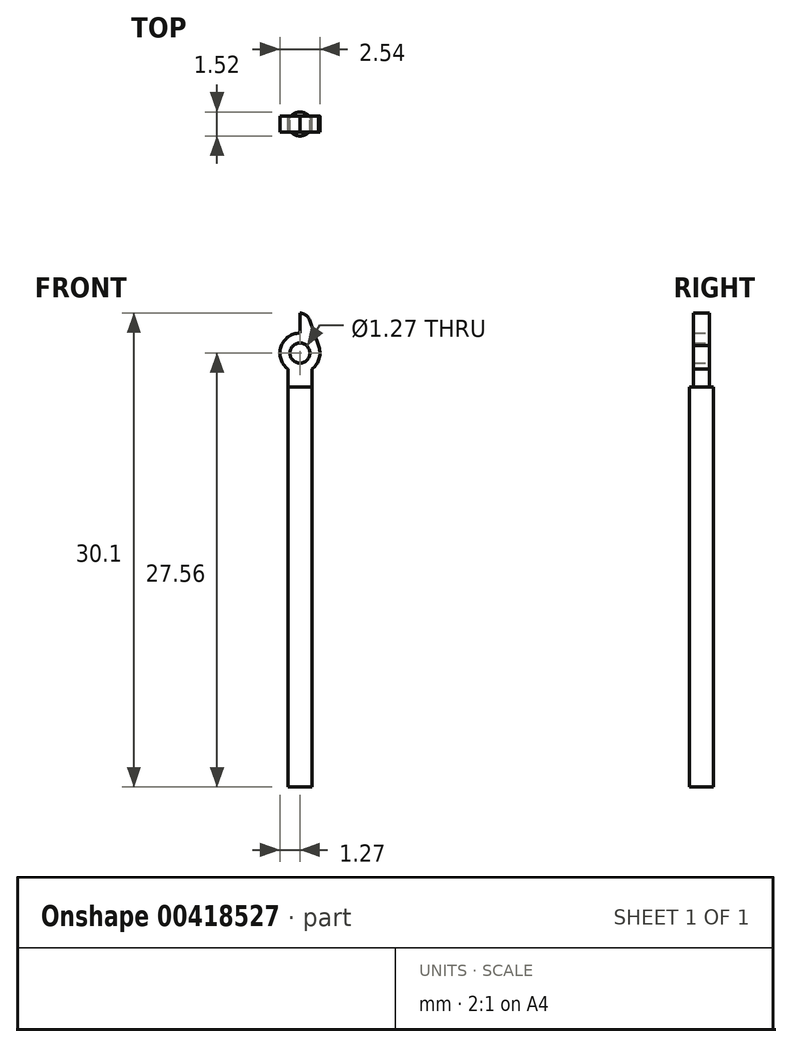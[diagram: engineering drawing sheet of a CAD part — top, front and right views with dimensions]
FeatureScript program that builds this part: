
annotation { "Feature Type Name" : "Feature", "Feature Type Description" : "" }
export const myFeature = defineFeature(function(context is Context, id is Id, definition is map)
    precondition{}
    {
        {
            var Q0;
            Q0=qCreatedBy(makeId("Front.planeOp"),FACE);
            var sketch = newSketch(context, id + "F0", { "sketchPlane" : qUnion([Q0])});
            skCircle(sketch, "E0", {"center": v(0, 0) * mm, "radius": 0.64 * mm});
            skCircle(sketch, "E1", {"center": v(0, 0) * mm, "radius": 1.27 * mm});
            skArc(sketch, "E2", {"start": v(0.6, 2.12) * mm, "mid": v(0.37, 2.42) * mm, "end": v(0, 2.54) * mm});
            skLineSegment(sketch, "E3", {"start": v(0, 2.54) * mm, "end": v(0, 1.27) * mm});
            skLineSegment(sketch, "E4", {"start": v(1.22, 0.35) * mm, "end": v(0.6, 2.12) * mm});
            skLineSegment(sketch, "E5", {"start": v(0.76, -2.16) * mm, "end": v(-0.76, -2.16) * mm});
            skLineSegment(sketch, "E6", {"start": v(0.76, -2.16) * mm, "end": v(0.76, -1.02) * mm});
            skLineSegment(sketch, "E7", {"start": v(-0.76, -2.16) * mm, "end": v(-0.76, -1.02) * mm});
            skSolve(sketch);
        }
        {
            var Q0;
            {var subQ0=sQuery(id+"F0.wireOp",EDGE,"E4");var subQ1=sQuery(id+"F0.wireOp",EDGE,"E1");var subQ2=makeQuery(id+"F0.imprint","INTERSECT",VERTEX,{"disambiguationData":[OD(0.0)],"derivedFrom":[subQ1,subQ0]});Q0=makeQuery(id+"F0.imprint","IMPRINT",FACE,{"disambiguationData":[TD([[makeQuery(id+"F0.imprint","IMPRINT",EDGE,{"disambiguationData":[TD([[subQ2,-1.0]])],"derivedFrom":subQ1}),1.0]])]});}
            var Q1;
            {var subQ4=sQuery(id+"F0.wireOp",EDGE,"E2");Q1=makeQuery(id+"F0.imprint","IMPRINT",FACE,{"disambiguationData":[TD([[makeQuery(id+"F0.imprint","IMPRINT",EDGE,{"derivedFrom":subQ4}),1.0]])]});}
            var Q2;
            Q2=makeQuery(id+"F0.imprint","IMPRINT",FACE,{"disambiguationData":[TD([[makeQuery(id+"F0.imprint","IMPRINT",EDGE,{"derivedFrom":sQuery(id+"F0.wireOp",EDGE,"E0")}),-1.0]])]});
            extrude(context, id + "F1", {"entities" : qUnion([Q0, Q1, Q2]), "endBound" : BoundingType.SYMMETRIC, "depth" : 1.02 * mm, "offsetDistance" : 25.4 * mm});
        }
        {
            var Q0;
            Q0=makeQuery(id+"F0.imprint","IMPRINT",FACE,{"disambiguationData":[TD([[makeQuery(id+"F0.imprint","IMPRINT",EDGE,{"derivedFrom":sQuery(id+"F0.wireOp",EDGE,"E5")}),-1.0]])]});
            extrude(context, id + "F2", {"entities" : qUnion([Q0]), "operationType" : NewBodyOperationType.ADD, "endBound" : BoundingType.SYMMETRIC, "depth" : 1.02 * mm, "offsetDistance" : 25.4 * mm});
        }
        {
            var Q0;
            Q0=makeQuery(id+"F2.opExtrude","SWEPT_FACE",FACE,{"disambiguationData":[OSD([sQuery(id+"F0.wireOp",EDGE,"E5")])]});
            var sketch = newSketch(context, id + "F3", { "sketchPlane" : qUnion([Q0])});
            skCircle(sketch, "E8", {"center": v(0, 0) * mm, "radius": 0.76 * mm});
            skSolve(sketch);
        }
        {
            var Q0;
            Q0 = qSketchRegion(id + "F3", true);
            extrude(context, id + "F4", {"entities" : qUnion([Q0]), "operationType" : NewBodyOperationType.ADD, "depth" : 25.4 * mm, "offsetDistance" : 25.4 * mm});
        }
    });
